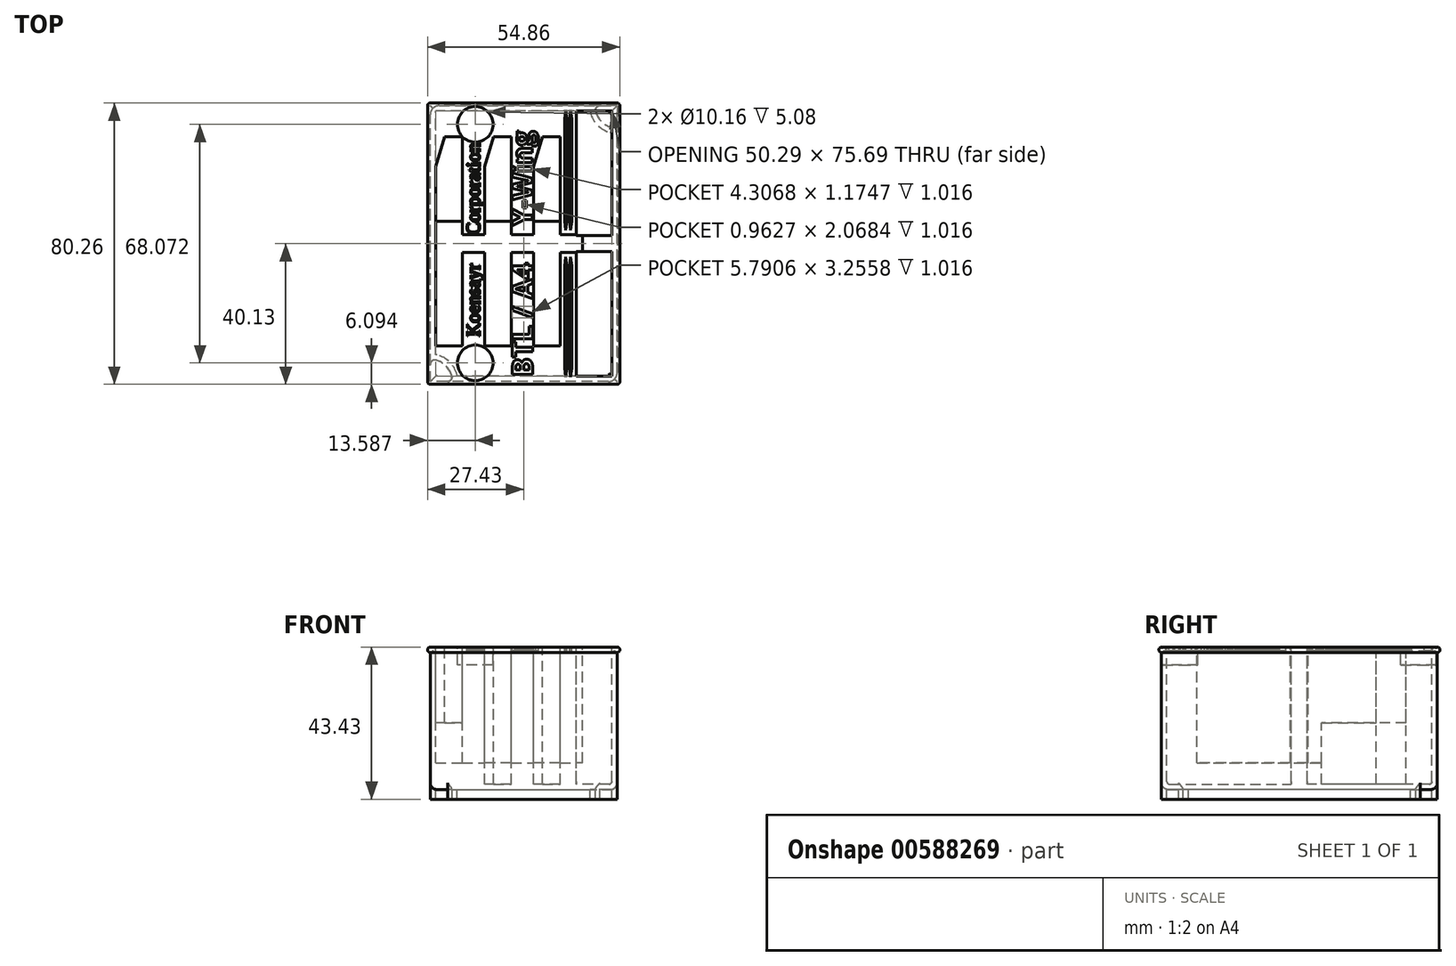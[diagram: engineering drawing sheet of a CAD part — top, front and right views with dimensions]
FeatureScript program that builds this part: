
annotation { "Feature Type Name" : "Feature", "Feature Type Description" : "" }
export const myFeature = defineFeature(function(context is Context, id is Id, definition is map)
    precondition{}
    {
        {
            var Q0;
            Q0=qCreatedBy(makeId("Front.planeOp"),FACE);
            var sketch = newSketch(context, id + "F0", { "sketchPlane" : qUnion([Q0])});
            skLineSegment(sketch, "E0.bottom", {"start": v(26.67, -20.32) * mm, "end": v(-26.67, -20.32) * mm});
            skLineSegment(sketch, "E0.top", {"start": v(26.67, 20.32) * mm, "end": v(-26.67, 20.32) * mm});
            skLineSegment(sketch, "E0.left", {"start": v(26.67, -20.32) * mm, "end": v(26.67, 20.32) * mm});
            skLineSegment(sketch, "E0.right", {"start": v(-26.67, -20.32) * mm, "end": v(-26.67, 20.32) * mm});
            skPoint(sketch, "E0.middle", {"position": v(0, 0) * mm});
            skSolve(sketch);
        }
        {
            var Q0;
            Q0=makeQuery(id+"F0.imprint","IMPRINT",FACE,{"disambiguationData":[TD([[makeQuery(id+"F0.imprint","IMPRINT",EDGE,{"derivedFrom":sQuery(id+"F0.wireOp",EDGE,"E0.bottom")}),-1.0]])]});
            extrude(context, id + "F1", {"entities" : qUnion([Q0]), "endBound" : BoundingType.SYMMETRIC, "depth" : 78.74 * mm});
        }
        {
            var Q0;
            Q0=makeQuery(id+"F1.opExtrude","SWEPT_FACE",FACE,{"disambiguationData":[OSD([sQuery(id+"F0.wireOp",EDGE,"E0.top")])]});
            shell(context, id + "F2", {"entities" : qUnion([Q0]), "thickness" : 1.52 * mm});
        }
        {
            var Q0;
            Q0=makeQuery(id+"F1.opExtrude","CAP_FACE",FACE,{"disambiguationData":[OSD([sQuery(id+"F0.wireOp",EDGE,"E0.bottom"),sQuery(id+"F0.wireOp",EDGE,"E0.top"),sQuery(id+"F0.wireOp",EDGE,"E0.left"),sQuery(id+"F0.wireOp",EDGE,"E0.right")])],"isStart":false});
            var sketch = newSketch(context, id + "F3", { "sketchPlane" : qUnion([Q0])});
            skArc(sketch, "E1", {"start": v(-26.67, 20.32) * mm, "mid": v(-27.43, 19.56) * mm, "end": v(-26.67, 18.8) * mm});
            skSolve(sketch);
        }
        {
            var Q0;
            {var subQ0=sQuery(id+"F3.wireOp",EDGE,"E1");Q0=makeQuery(id+"F3.imprint","IMPRINT",FACE,{"disambiguationData":[TD([[makeQuery(id+"F3.imprint","IMPRINT",EDGE,{"derivedFrom":subQ0}),1.0]])]});}
            var Q1;
            Q1=makeQuery(id+"F1.opExtrude","SWEPT_EDGE",EDGE,{"disambiguationData":[OSD([sQuery(id+"F0.wireOp",EDGE,"E0.top"),sQuery(id+"F0.wireOp",EDGE,"E0.right")])]});
            var Q2;
            Q2=makeQuery(id+"F1.opExtrude","CAP_EDGE",EDGE,{"disambiguationData":[OSD([sQuery(id+"F0.wireOp",EDGE,"E0.top")])],"isStart":true});
            var Q3;
            Q3=makeQuery(id+"F1.opExtrude","SWEPT_EDGE",EDGE,{"disambiguationData":[OSD([sQuery(id+"F0.wireOp",EDGE,"E0.top"),sQuery(id+"F0.wireOp",EDGE,"E0.left")])]});
            var Q4;
            Q4=makeQuery(id+"F1.opExtrude","CAP_EDGE",EDGE,{"disambiguationData":[OSD([sQuery(id+"F0.wireOp",EDGE,"E0.top")])],"isStart":false});
            sweep(context, id + "F4", {"operationType" : NewBodyOperationType.ADD, "profiles" : qUnion([Q0]), "path" : qUnion([Q1, Q2, Q3, Q4])});
        }
        {
            var Q0;
            Q0=makeQuery(id+"F1.opExtrude","SWEPT_FACE",FACE,{"disambiguationData":[OSD([sQuery(id+"F0.wireOp",EDGE,"E0.bottom")])]});
            var sketch = newSketch(context, id + "F5", { "sketchPlane" : qUnion([Q0])});
            skLineSegment(sketch, "E2.bottom", {"start": v(26.67, 39.37) * mm, "end": v(21.75, 39.37) * mm});
            skLineSegment(sketch, "E2.left", {"start": v(26.67, 39.37) * mm, "end": v(26.67, 34.45) * mm});
            skPoint(sketch, "E3.newPointA", {"position": v(20.32, 19.05) * mm});
            skArc(sketch, "E4", {"start": v(20.52, 37.78) * mm, "mid": v(22.18, 34.88) * mm, "end": v(25.08, 33.22) * mm});
            skPoint(sketch, "E5.visualSharp", {"position": v(20.32, 39.37) * mm});
            skArc(sketch, "E5.filletArc", {"start": v(21.75, 39.37) * mm, "mid": v(20.75, 38.88) * mm, "end": v(20.52, 37.78) * mm});
            skPoint(sketch, "E6.visualSharp", {"position": v(26.67, 33.02) * mm});
            skArc(sketch, "E6.filletArc", {"start": v(25.08, 33.22) * mm, "mid": v(26.18, 33.45) * mm, "end": v(26.67, 34.45) * mm});
            skArc(sketch, "E7.MirrorCS", {"start": v(-21.75, 39.37) * mm, "mid": v(-20.75, 38.88) * mm, "end": v(-20.52, 37.78) * mm});
            skArc(sketch, "E8.MirrorCS", {"start": v(-20.52, 37.78) * mm, "mid": v(-22.18, 34.88) * mm, "end": v(-25.08, 33.22) * mm});
            skArc(sketch, "E9.MirrorCS", {"start": v(-25.08, 33.22) * mm, "mid": v(-26.18, 33.45) * mm, "end": v(-26.67, 34.45) * mm});
            skLineSegment(sketch, "E10.MirrorCS", {"start": v(-26.67, 39.37) * mm, "end": v(-26.67, 34.45) * mm});
            skLineSegment(sketch, "E11.MirrorCS", {"start": v(-26.67, 39.37) * mm, "end": v(-21.75, 39.37) * mm});
            skArc(sketch, "E12.MirrorCS", {"start": v(-20.52, -37.78) * mm, "mid": v(-22.18, -34.88) * mm, "end": v(-25.08, -33.22) * mm});
            skArc(sketch, "E13.MirrorCS", {"start": v(-21.75, -39.37) * mm, "mid": v(-20.75, -38.88) * mm, "end": v(-20.52, -37.78) * mm});
            skLineSegment(sketch, "E14.MirrorCS", {"start": v(-26.67, -39.37) * mm, "end": v(-21.75, -39.37) * mm});
            skLineSegment(sketch, "E15.MirrorCS", {"start": v(-26.67, -39.37) * mm, "end": v(-26.67, -34.45) * mm});
            skArc(sketch, "E16.MirrorCS", {"start": v(-25.08, -33.22) * mm, "mid": v(-26.18, -33.45) * mm, "end": v(-26.67, -34.45) * mm});
            skArc(sketch, "E17.MirrorCS", {"start": v(21.75, -39.37) * mm, "mid": v(20.75, -38.88) * mm, "end": v(20.52, -37.78) * mm});
            skArc(sketch, "E18.MirrorCS", {"start": v(20.52, -37.78) * mm, "mid": v(22.18, -34.88) * mm, "end": v(25.08, -33.22) * mm});
            skArc(sketch, "E19.MirrorCS", {"start": v(25.08, -33.22) * mm, "mid": v(26.18, -33.45) * mm, "end": v(26.67, -34.45) * mm});
            skLineSegment(sketch, "E20.MirrorCS", {"start": v(26.67, -39.37) * mm, "end": v(26.67, -34.45) * mm});
            skLineSegment(sketch, "E21.MirrorCS", {"start": v(26.67, -39.37) * mm, "end": v(21.75, -39.37) * mm});
            skSolve(sketch);
        }
        {
            var Q0;
            Q0=makeQuery(id+"F5.imprint","IMPRINT",FACE,{"disambiguationData":[TD([[makeQuery(id+"F5.imprint","IMPRINT",EDGE,{"derivedFrom":sQuery(id+"F5.wireOp",EDGE,"E2.bottom")}),1.0]])]});
            var Q1;
            Q1=makeQuery(id+"F5.imprint","IMPRINT",FACE,{"disambiguationData":[TD([[makeQuery(id+"F5.imprint","IMPRINT",EDGE,{"derivedFrom":sQuery(id+"F5.wireOp",EDGE,"E8.MirrorCS")}),-1.0]])]});
            var Q2;
            Q2=makeQuery(id+"F5.imprint","IMPRINT",FACE,{"disambiguationData":[TD([[makeQuery(id+"F5.imprint","IMPRINT",EDGE,{"derivedFrom":sQuery(id+"F5.wireOp",EDGE,"E12.MirrorCS")}),1.0]])]});
            var Q3;
            Q3=makeQuery(id+"F5.imprint","IMPRINT",FACE,{"disambiguationData":[TD([[makeQuery(id+"F5.imprint","IMPRINT",EDGE,{"derivedFrom":sQuery(id+"F5.wireOp",EDGE,"E17.MirrorCS")}),-1.0]])]});
            extrude(context, id + "F6", {"entities" : qUnion([Q0, Q1, Q2, Q3]), "operationType" : NewBodyOperationType.ADD, "depth" : 2.8 * mm});
        }
        {
            var Q0;
            Q0=makeQuery(id+"F6.opExtrude","CAP_FACE",FACE,{"disambiguationData":[OSD([sQuery(id+"F5.wireOp",EDGE,"E2.bottom"),sQuery(id+"F5.wireOp",EDGE,"E2.left"),sQuery(id+"F5.wireOp",EDGE,"E4"),sQuery(id+"F5.wireOp",EDGE,"E5.filletArc"),sQuery(id+"F5.wireOp",EDGE,"E6.filletArc")])],"isStart":false});
            var Q1;
            Q1=makeQuery(id+"F6.opExtrude","CAP_FACE",FACE,{"disambiguationData":[OSD([sQuery(id+"F5.wireOp",EDGE,"E8.MirrorCS"),sQuery(id+"F5.wireOp",EDGE,"E9.MirrorCS"),sQuery(id+"F5.wireOp",EDGE,"E10.MirrorCS"),sQuery(id+"F5.wireOp",EDGE,"E7.MirrorCS"),sQuery(id+"F5.wireOp",EDGE,"E11.MirrorCS")])],"isStart":false});
            var Q2;
            Q2=makeQuery(id+"F6.opExtrude","CAP_FACE",FACE,{"disambiguationData":[OSD([sQuery(id+"F5.wireOp",EDGE,"E12.MirrorCS"),sQuery(id+"F5.wireOp",EDGE,"E13.MirrorCS"),sQuery(id+"F5.wireOp",EDGE,"E14.MirrorCS"),sQuery(id+"F5.wireOp",EDGE,"E15.MirrorCS"),sQuery(id+"F5.wireOp",EDGE,"E16.MirrorCS")])],"isStart":false});
            var Q3;
            Q3=makeQuery(id+"F6.opExtrude","CAP_FACE",FACE,{"disambiguationData":[OSD([sQuery(id+"F5.wireOp",EDGE,"E17.MirrorCS"),sQuery(id+"F5.wireOp",EDGE,"E18.MirrorCS"),sQuery(id+"F5.wireOp",EDGE,"E19.MirrorCS"),sQuery(id+"F5.wireOp",EDGE,"E20.MirrorCS"),sQuery(id+"F5.wireOp",EDGE,"E21.MirrorCS")])],"isStart":false});
            shell(context, id + "F7", {"entities" : qUnion([Q0, Q1, Q2, Q3]), "thickness" : 1.52 * mm});
        }
        {
            var Q0;
            Q0=makeQuery(id+"F2.opShell","OFFSET_FACE",FACE,{"disambiguationData":[OSD([sQuery(id+"F0.wireOp",EDGE,"E0.bottom")])]});
            fillet(context, id + "F8", {"entities" : qUnion([Q0]), "radius" : 0.76 * mm, "tangentPropagation" : true, "allowEdgeOverflow" : false});
        }
        {
            var Q0;
            Q0=makeQuery(id+"F1.opExtrude","SWEPT_EDGE",EDGE,{"disambiguationData":[OSD([sQuery(id+"F0.wireOp",EDGE,"E0.bottom"),sQuery(id+"F0.wireOp",EDGE,"E0.right")])]});
            var Q1;
            Q1=makeQuery(id+"F1.opExtrude","CAP_EDGE",EDGE,{"disambiguationData":[OSD([sQuery(id+"F0.wireOp",EDGE,"E0.bottom")])],"isStart":false});
            var Q2;
            Q2=makeQuery(id+"F1.opExtrude","SWEPT_EDGE",EDGE,{"disambiguationData":[OSD([sQuery(id+"F0.wireOp",EDGE,"E0.bottom"),sQuery(id+"F0.wireOp",EDGE,"E0.left")])]});
            var Q3;
            Q3=makeQuery(id+"F1.opExtrude","CAP_EDGE",EDGE,{"disambiguationData":[OSD([sQuery(id+"F0.wireOp",EDGE,"E0.bottom")])],"isStart":true});
            fillet(context, id + "F9", {"entities" : qUnion([Q0, Q1, Q2, Q3]), "radius" : 1.9 * mm, "tangentPropagation" : true, "allowEdgeOverflow" : false});
        }
        {
            var Q0;
            Q0=makeQuery(id+"F4.opSweep","MID_CAP_EDGE",EDGE,{"disambiguationData":[OSD([sQuery(id+"F0.wireOp",EDGE,"E0.top"),sQuery(id+"F0.wireOp",EDGE,"E0.left"),sQuery(id+"F3.wireOp",EDGE,"E1")])],"capPos":3.0});
            var Q1;
            Q1=makeQuery(id+"F4.opSweep","MID_CAP_EDGE",EDGE,{"disambiguationData":[OSD([sQuery(id+"F0.wireOp",EDGE,"E0.top"),sQuery(id+"F0.wireOp",EDGE,"E0.left"),sQuery(id+"F3.wireOp",EDGE,"E1")])],"capPos":2.0});
            var Q2;
            Q2=makeQuery(id+"F4.opSweep","MID_CAP_EDGE",EDGE,{"disambiguationData":[OSD([sQuery(id+"F0.wireOp",EDGE,"E0.top"),sQuery(id+"F0.wireOp",EDGE,"E0.right"),sQuery(id+"F3.wireOp",EDGE,"E1")])],"capPos":1.0});
            var Q3;
            Q3=makeQuery(id+"F4.opSweep","CAP_EDGE",EDGE,{"disambiguationData":[OSD([sQuery(id+"F0.wireOp",EDGE,"E0.top"),sQuery(id+"F0.wireOp",EDGE,"E0.right"),sQuery(id+"F3.wireOp",EDGE,"E1")])],"isStart":true});
            fillet(context, id + "F10", {"entities" : qUnion([Q0, Q1, Q2, Q3]), "radius" : 0.76 * mm, "tangentPropagation" : true, "allowEdgeOverflow" : false});
        }
        {
            var Q0;
            Q0=makeQuery(id+"F6.boolean.opBoolean","MERGE",EDGE,{"derivedFrom":[makeQuery(id+"F1.opExtrude","CAP_EDGE",EDGE,{"disambiguationData":[OSD([sQuery(id+"F0.wireOp",EDGE,"E0.left")])],"isStart":false}),makeQuery(id+"F6.opExtrude","SWEPT_EDGE",EDGE,{"disambiguationData":[OSD([sQuery(id+"F5.wireOp",EDGE,"E2.bottom"),sQuery(id+"F5.wireOp",EDGE,"E2.left")])]})]});
            var Q1;
            Q1=makeQuery(id+"F6.boolean.opBoolean","MERGE",EDGE,{"derivedFrom":[makeQuery(id+"F1.opExtrude","CAP_EDGE",EDGE,{"disambiguationData":[OSD([sQuery(id+"F0.wireOp",EDGE,"E0.left")])],"isStart":true}),makeQuery(id+"F6.opExtrude","SWEPT_EDGE",EDGE,{"disambiguationData":[OSD([sQuery(id+"F5.wireOp",EDGE,"E20.MirrorCS"),sQuery(id+"F5.wireOp",EDGE,"E21.MirrorCS")])]})]});
            var Q2;
            Q2=makeQuery(id+"F6.boolean.opBoolean","MERGE",EDGE,{"derivedFrom":[makeQuery(id+"F1.opExtrude","CAP_EDGE",EDGE,{"disambiguationData":[OSD([sQuery(id+"F0.wireOp",EDGE,"E0.right")])],"isStart":false}),makeQuery(id+"F6.opExtrude","SWEPT_EDGE",EDGE,{"disambiguationData":[OSD([sQuery(id+"F5.wireOp",EDGE,"E10.MirrorCS"),sQuery(id+"F5.wireOp",EDGE,"E11.MirrorCS")])]})]});
            var Q3;
            Q3=makeQuery(id+"F6.boolean.opBoolean","MERGE",EDGE,{"derivedFrom":[makeQuery(id+"F1.opExtrude","CAP_EDGE",EDGE,{"disambiguationData":[OSD([sQuery(id+"F0.wireOp",EDGE,"E0.right")])],"isStart":true}),makeQuery(id+"F6.opExtrude","SWEPT_EDGE",EDGE,{"disambiguationData":[OSD([sQuery(id+"F5.wireOp",EDGE,"E14.MirrorCS"),sQuery(id+"F5.wireOp",EDGE,"E15.MirrorCS")])]})]});
            fillet(context, id + "F11", {"entities" : qUnion([Q0, Q1, Q2, Q3]), "radius" : 2.54 * mm, "tangentPropagation" : true, "allowEdgeOverflow" : false});
        }
        {
            var Q0;
            Q0=makeQuery(id+"F1.opExtrude","SWEPT_BODY",BODY,{"disambiguationData":[OSD([sQuery(id+"F0.wireOp",EDGE,"E0.bottom"),sQuery(id+"F0.wireOp",EDGE,"E0.top"),sQuery(id+"F0.wireOp",EDGE,"E0.left"),sQuery(id+"F0.wireOp",EDGE,"E0.right")])]});
            transform(context, id + "F12", {"entities" : qUnion([Q0]), "transformType" : TransformType.COPY});
        }
        {
            var Q0;
            Q0=makeQuery(id+"F12.opPattern","COPY",BODY,{"derivedFrom":makeQuery(id+"F1.opExtrude","SWEPT_BODY",BODY,{"disambiguationData":[OSD([sQuery(id+"F0.wireOp",EDGE,"E0.bottom"),sQuery(id+"F0.wireOp",EDGE,"E0.top"),sQuery(id+"F0.wireOp",EDGE,"E0.left"),sQuery(id+"F0.wireOp",EDGE,"E0.right")])]}),"instanceName":"1"});
            deleteBodies(context, id + "F13", {"entities" : qUnion([Q0])});
        }
        {
            var Q0;
            Q0=makeQuery(id+"F1.opExtrude","SWEPT_FACE",FACE,{"disambiguationData":[OSD([sQuery(id+"F0.wireOp",EDGE,"E0.top")])]});
            var sketch = newSketch(context, id + "F14", { "sketchPlane" : qUnion([Q0])});
            skPoint(sketch, "E22", {"position": v(-25.15, 30.48) * mm});
            skLineSegment(sketch, "E23.bottom", {"start": v(-22.6, 30.48) * mm, "end": v(-17.53, 30.48) * mm});
            skLineSegment(sketch, "E23.top", {"start": v(-25.15, -29.21) * mm, "end": v(-17.53, -29.21) * mm});
            skLineSegment(sketch, "E23.left", {"start": v(-25.15, 21.96) * mm, "end": v(-25.15, -29.21) * mm});
            skLineSegment(sketch, "E23.right", {"start": v(-17.53, 30.48) * mm, "end": v(-17.53, 2.54) * mm});
            skLineSegment(sketch, "E24.bottom", {"start": v(-17.53, 2.54) * mm, "end": v(-11.18, 2.54) * mm});
            skLineSegment(sketch, "E24.top", {"start": v(-17.53, -2.54) * mm, "end": v(-11.18, -2.54) * mm});
            skLineSegment(sketch, "E24.right", {"start": v(-11.18, 2.54) * mm, "end": v(-11.18, -2.54) * mm});
            skLineSegment(sketch, "E25.trimOffspring", {"start": v(-17.53, -2.54) * mm, "end": v(-17.53, -29.21) * mm});
            skLineSegment(sketch, "E26", {"start": v(-17.53, 2.54) * mm, "end": v(-17.53, 6.35) * mm});
            skLineSegment(sketch, "E27", {"start": v(-17.53, 6.35) * mm, "end": v(-25.15, 6.35) * mm});
            skPoint(sketch, "E28", {"position": v(-11.18, 30.48) * mm});
            skLineSegment(sketch, "E29.bottom", {"start": v(-8.64, 30.48) * mm, "end": v(-3.56, 30.48) * mm});
            skLineSegment(sketch, "E29.top", {"start": v(-11.18, -29.2) * mm, "end": v(-3.56, -29.2) * mm});
            skLineSegment(sketch, "E29.left", {"start": v(-11.18, 21.96) * mm, "end": v(-11.18, -29.2) * mm});
            skLineSegment(sketch, "E29.right", {"start": v(-3.56, 30.48) * mm, "end": v(-3.56, 2.54) * mm});
            skLineSegment(sketch, "E30.bottom", {"start": v(-3.56, 2.54) * mm, "end": v(2.8, 2.54) * mm});
            skLineSegment(sketch, "E30.top", {"start": v(-3.56, -2.54) * mm, "end": v(2.8, -2.54) * mm});
            skLineSegment(sketch, "E30.right", {"start": v(2.8, 2.54) * mm, "end": v(2.8, -2.54) * mm});
            skLineSegment(sketch, "E31.trimOffspring", {"start": v(-3.56, -2.54) * mm, "end": v(-3.56, -29.2) * mm});
            skLineSegment(sketch, "E32", {"start": v(-3.56, 2.54) * mm, "end": v(-3.56, 6.35) * mm});
            skLineSegment(sketch, "E33", {"start": v(-3.56, 6.35) * mm, "end": v(-11.18, 6.35) * mm});
            skPoint(sketch, "E34", {"position": v(2.8, 30.48) * mm});
            skLineSegment(sketch, "E35.bottom", {"start": v(5.33, 30.48) * mm, "end": v(10.41, 30.48) * mm});
            skLineSegment(sketch, "E35.top", {"start": v(2.8, -29.2) * mm, "end": v(10.41, -29.2) * mm});
            skLineSegment(sketch, "E35.left", {"start": v(2.8, 21.96) * mm, "end": v(2.8, -29.2) * mm});
            skLineSegment(sketch, "E35.right", {"start": v(10.41, 30.48) * mm, "end": v(10.41, 2.54) * mm});
            skLineSegment(sketch, "E36.bottom", {"start": v(10.41, 2.54) * mm, "end": v(16.76, 2.54) * mm});
            skLineSegment(sketch, "E36.top", {"start": v(10.41, -2.54) * mm, "end": v(16.76, -2.54) * mm});
            skLineSegment(sketch, "E37.trimOffspring", {"start": v(10.41, -2.54) * mm, "end": v(10.41, -29.2) * mm});
            skLineSegment(sketch, "E38", {"start": v(10.41, 2.54) * mm, "end": v(10.41, 6.35) * mm});
            skLineSegment(sketch, "E39", {"start": v(10.41, 6.35) * mm, "end": v(2.8, 6.35) * mm});
            skLineSegment(sketch, "E40", {"start": v(16.76, 2.54) * mm, "end": v(16.76, -2.54) * mm});
            skPoint(sketch, "E41.0", {"position": v(25.15, 37.85) * mm});
            skPoint(sketch, "E41.1", {"position": v(25.15, -37.85) * mm});
            skLineSegment(sketch, "E42.bottom", {"start": v(25.15, 37.85) * mm, "end": v(14.99, 37.85) * mm});
            skLineSegment(sketch, "E42.top", {"start": v(25.15, 2.29) * mm, "end": v(14.99, 2.29) * mm});
            skLineSegment(sketch, "E42.left", {"start": v(25.15, 37.85) * mm, "end": v(25.15, 2.29) * mm});
            skLineSegment(sketch, "E42.right", {"start": v(14.99, 37.85) * mm, "end": v(14.99, 2.29) * mm});
            skLineSegment(sketch, "E43.bottom", {"start": v(25.15, -37.85) * mm, "end": v(14.99, -37.85) * mm});
            skLineSegment(sketch, "E43.top", {"start": v(25.15, -2.29) * mm, "end": v(14.99, -2.29) * mm});
            skLineSegment(sketch, "E43.left", {"start": v(25.15, -37.85) * mm, "end": v(25.15, -2.29) * mm});
            skLineSegment(sketch, "E43.right", {"start": v(14.99, -37.85) * mm, "end": v(14.99, -2.29) * mm});
            skPoint(sketch, "E44.middle", {"position": v(0, 0.64) * mm});
            skLineSegment(sketch, "E45.0", {"start": v(25.15, -37.85) * mm, "end": v(-25.15, -37.85) * mm});
            skLineSegment(sketch, "E46", {"start": v(-17.53, 30.48) * mm, "end": v(-22.6, 30.48) * mm});
            skLineSegment(sketch, "E47", {"start": v(-22.6, 30.48) * mm, "end": v(-25.15, 21.96) * mm});
            skLineSegment(sketch, "E48", {"start": v(-3.56, 30.48) * mm, "end": v(-7.37, 30.48) * mm});
            skLineSegment(sketch, "E49", {"start": v(-3.56, 30.48) * mm, "end": v(-8.64, 30.48) * mm});
            skLineSegment(sketch, "E50", {"start": v(-8.64, 30.48) * mm, "end": v(-11.18, 21.96) * mm});
            skLineSegment(sketch, "E51", {"start": v(10.41, 30.48) * mm, "end": v(5.33, 30.48) * mm});
            skLineSegment(sketch, "E52", {"start": v(5.33, 30.48) * mm, "end": v(2.8, 21.96) * mm});
            skLineSegment(sketch, "E53.bottom", {"start": v(-25.15, -37.85) * mm, "end": v(25.15, -37.85) * mm});
            skLineSegment(sketch, "E53.top", {"start": v(-25.15, 37.85) * mm, "end": v(25.15, 37.85) * mm});
            skLineSegment(sketch, "E53.left", {"start": v(-25.15, -37.85) * mm, "end": v(-25.15, 37.85) * mm});
            skLineSegment(sketch, "E53.right", {"start": v(25.15, -37.85) * mm, "end": v(25.15, 37.85) * mm});
            skSolve(sketch);
        }
        {
            var Q0;
            Q0=makeQuery(id+"F14.imprint","IMPRINT",FACE,{"disambiguationData":[TD([[makeQuery(id+"F14.imprint","IMPRINT",EDGE,{"derivedFrom":sQuery(id+"F14.wireOp",EDGE,"E23.right")}),1.0]])]});
            var Q1;
            {var subQ6=sQuery(id+"F14.wireOp",EDGE,"E23.top");Q1=makeQuery(id+"F14.imprint","IMPRINT",FACE,{"disambiguationData":[TD([[makeQuery(id+"F14.imprint","IMPRINT",EDGE,{"derivedFrom":subQ6}),-1.0]])]});}
            var Q2;
            Q2=makeQuery(id+"F14.imprint","IMPRINT",FACE,{"disambiguationData":[TD([[makeQuery(id+"F14.imprint","IMPRINT",EDGE,{"derivedFrom":sQuery(id+"F14.wireOp",EDGE,"E23.right")}),-1.0]])]});
            var Q3;
            {var subQ1=sQuery(id+"F14.wireOp",EDGE,"E29.right");Q3=makeQuery(id+"F14.imprint","IMPRINT",FACE,{"disambiguationData":[TD([[makeQuery(id+"F14.imprint","IMPRINT",EDGE,{"derivedFrom":subQ1}),-1.0]])]});}
            var Q4;
            Q4=makeQuery(id+"F14.imprint","IMPRINT",FACE,{"disambiguationData":[TD([[makeQuery(id+"F14.imprint","IMPRINT",EDGE,{"derivedFrom":sQuery(id+"F14.wireOp",EDGE,"E35.right")}),-1.0]])]});
            var Q5;
            {var subQ4=sQuery(id+"F14.wireOp",EDGE,"E35.top");Q5=makeQuery(id+"F14.imprint","IMPRINT",FACE,{"disambiguationData":[TD([[makeQuery(id+"F14.imprint","IMPRINT",EDGE,{"derivedFrom":subQ4}),1.0]])]});}
            var Q6;
            {var subQ1=sQuery(id+"F14.wireOp",EDGE,"E23.top");Q6=makeQuery(id+"F14.imprint","IMPRINT",FACE,{"disambiguationData":[TD([[makeQuery(id+"F14.imprint","IMPRINT",EDGE,{"derivedFrom":subQ1}),1.0]])]});}
            var Q7;
            {var subQ0=sQuery(id+"F14.wireOp",EDGE,"E40");Q7=makeQuery(id+"F14.imprint","IMPRINT",FACE,{"disambiguationData":[TD([[makeQuery(id+"F14.imprint","IMPRINT",EDGE,{"derivedFrom":subQ0}),1.0]])]});}
            var Q8;
            {var subQ2=sQuery(id+"F14.wireOp",EDGE,"E29.top");Q8=makeQuery(id+"F14.imprint","IMPRINT",FACE,{"disambiguationData":[TD([[makeQuery(id+"F14.imprint","IMPRINT",EDGE,{"derivedFrom":subQ2}),1.0]])]});}
            extrude(context, id + "F15", {"entities" : qUnion([Q0, Q1, Q2, Q3, Q4, Q5, Q6, Q7, Q8]), "operationType" : NewBodyOperationType.ADD, "endBound" : BoundingType.UP_TO_NEXT, "oppositeDirection" : true, "depth" : 25.4 * mm, "offsetDistance" : 25.4 * mm});
        }
        {
            var Q0;
            {var subQ1=sQuery(id+"F14.wireOp",EDGE,"E23.top");Q0=makeQuery(id+"F14.imprint","IMPRINT",FACE,{"disambiguationData":[TD([[makeQuery(id+"F14.imprint","IMPRINT",EDGE,{"derivedFrom":subQ1}),1.0]])]});}
            var Q1;
            {var subQ2=sQuery(id+"F14.wireOp",EDGE,"E29.top");Q1=makeQuery(id+"F14.imprint","IMPRINT",FACE,{"disambiguationData":[TD([[makeQuery(id+"F14.imprint","IMPRINT",EDGE,{"derivedFrom":subQ2}),1.0]])]});}
            var Q2;
            {var subQ4=sQuery(id+"F14.wireOp",EDGE,"E35.top");Q2=makeQuery(id+"F14.imprint","IMPRINT",FACE,{"disambiguationData":[TD([[makeQuery(id+"F14.imprint","IMPRINT",EDGE,{"derivedFrom":subQ4}),1.0]])]});}
            extrude(context, id + "F16", {"entities" : qUnion([Q0, Q1, Q2]), "operationType" : NewBodyOperationType.REMOVE, "oppositeDirection" : true, "depth" : 33.02 * mm, "offsetDistance" : 25.4 * mm});
        }
        {
            var Q0;
            Q0=makeQuery(id+"F14.imprint","IMPRINT",FACE,{"disambiguationData":[TD([[makeQuery(id+"F14.imprint","IMPRINT",EDGE,{"derivedFrom":sQuery(id+"F14.wireOp",EDGE,"E23.right")}),-1.0]])]});
            var Q1;
            {var subQ1=sQuery(id+"F14.wireOp",EDGE,"E29.right");Q1=makeQuery(id+"F14.imprint","IMPRINT",FACE,{"disambiguationData":[TD([[makeQuery(id+"F14.imprint","IMPRINT",EDGE,{"derivedFrom":subQ1}),-1.0]])]});}
            var Q2;
            Q2=makeQuery(id+"F14.imprint","IMPRINT",FACE,{"disambiguationData":[TD([[makeQuery(id+"F14.imprint","IMPRINT",EDGE,{"derivedFrom":sQuery(id+"F14.wireOp",EDGE,"E35.right")}),-1.0]])]});
            extrude(context, id + "F17", {"entities" : qUnion([Q0, Q1, Q2]), "operationType" : NewBodyOperationType.REMOVE, "oppositeDirection" : true, "depth" : 21.59 * mm, "offsetDistance" : 25.4 * mm});
        }
        {
            var Q0;
            Q0=makeQuery(id+"F15.boolean.opBoolean","MERGE",FACE,{"derivedFrom":[makeQuery(id+"F1.opExtrude","SWEPT_FACE",FACE,{"disambiguationData":[OSD([sQuery(id+"F0.wireOp",EDGE,"E0.top")])]}),makeQuery(id+"F15.opExtrude","CAP_FACE",FACE,{"disambiguationData":[OSD([sQuery(id+"F14.wireOp",EDGE,"E42.top"),sQuery(id+"F14.wireOp",EDGE,"E42.right"),sQuery(id+"F14.wireOp",EDGE,"E43.top"),sQuery(id+"F14.wireOp",EDGE,"E43.right"),sQuery(id+"F14.wireOp",EDGE,"E53.bottom"),sQuery(id+"F14.wireOp",EDGE,"E53.top"),sQuery(id+"F14.wireOp",EDGE,"E53.left"),sQuery(id+"F14.wireOp",EDGE,"E53.right")])],"isStart":true})]});
            var sketch = newSketch(context, id + "F18", { "sketchPlane" : qUnion([Q0])});
            skLineSegment(sketch, "E54.0", {"start": v(26.92, -39.37) * mm, "end": v(-26.42, -39.37) * mm});
            skLineSegment(sketch, "E55.2", {"start": v(26.67, 39.37) * mm, "end": v(-26.67, 39.37) * mm});
            skCircle(sketch, "E56", {"center": v(-13.84, -34.04) * mm, "radius": 5.08 * mm});
            skCircle(sketch, "E57", {"center": v(-13.84, 34.04) * mm, "radius": 5.08 * mm});
            skSolve(sketch);
        }
        {
            var Q0;
            Q0 = qSketchRegion(id + "F18", true);
            extrude(context, id + "F19", {"entities" : qUnion([Q0]), "operationType" : NewBodyOperationType.REMOVE, "oppositeDirection" : true, "depth" : 5.08 * mm, "offsetDistance" : 25.4 * mm});
        }
        {
            var Q0;
            Q0=makeQuery(id+"F15.boolean.opBoolean","MERGE",FACE,{"derivedFrom":[makeQuery(id+"F1.opExtrude","SWEPT_FACE",FACE,{"disambiguationData":[OSD([sQuery(id+"F0.wireOp",EDGE,"E0.top")])]}),makeQuery(id+"F15.opExtrude","CAP_FACE",FACE,{"disambiguationData":[OSD([sQuery(id+"F14.wireOp",EDGE,"E42.top"),sQuery(id+"F14.wireOp",EDGE,"E42.right"),sQuery(id+"F14.wireOp",EDGE,"E43.top"),sQuery(id+"F14.wireOp",EDGE,"E43.right"),sQuery(id+"F14.wireOp",EDGE,"E53.bottom"),sQuery(id+"F14.wireOp",EDGE,"E53.top"),sQuery(id+"F14.wireOp",EDGE,"E53.left"),sQuery(id+"F14.wireOp",EDGE,"E53.right")])],"isStart":true})]});
            var sketch = newSketch(context, id + "F20", { "sketchPlane" : qUnion([Q0])});
            skText(sketch, "E58", { "text": "Y-Wing", "fontName": "OpenSans-Bold.ttf"});
            skText(sketch, "E59", { "text": "BTL / A4", "fontName": "OpenSans-Bold.ttf"});
            skText(sketch, "E60", { "text": "Y-Wing", "fontName": "OpenSans-Bold.ttf"});
            skText(sketch, "E61", { "text": "Koensayr", "fontName": "Tinos-Regular.ttf"});
            skText(sketch, "E62", { "text": "Corporation", "fontName": "Tinos-Regular.ttf"});
            skPoint(sketch, "E63.endSnap0", {"position": v(-14.55, -23.65) * mm});
            const initialGuessF20  = {"E58": [0.0026, 0.06217, 0, 1, 0.00574], "E59": [0.00254, -0.03801, 0, 1, 0.00584], "E60": [0.00238, 0.00508, 0, 1, 0.00568], "E61": [-0.0126, -0.02651, 0, 1, 0.00391], "E62": [-0.0126, 0.00254, 0, 1, 0.00391]};
            skSetInitialGuess(sketch, initialGuessF20);
            skSolve(sketch);
        }
        {
            var Q0;
            Q0 = qSketchRegion(id + "F20", true);
            extrude(context, id + "F21", {"entities" : qUnion([Q0]), "operationType" : NewBodyOperationType.REMOVE, "oppositeDirection" : true, "depth" : 1.02 * mm, "offsetDistance" : 25.4 * mm});
        }
        {
            var Q0;
            {var subQ0=sQuery(id+"F14.wireOp",EDGE,"E43.right");var subQ1=sQuery(id+"F14.wireOp",EDGE,"E43.top");var subQ2=sQuery(id+"F14.wireOp",EDGE,"E42.right");var subQ3=sQuery(id+"F14.wireOp",EDGE,"E42.top");var subQ6=sQuery(id+"F0.wireOp",EDGE,"E0.top");var subQ8=sQuery(id+"F0.wireOp",EDGE,"E0.left");var subQ17=sQuery(id+"F14.wireOp",EDGE,"E53.left");Q0=makeQuery(id+"F21.boolean.opBoolean","SPLIT",FACE,{"disambiguationData":[TD([makeQuery(id+"F2.opShell","OFFSET_FACE",FACE,{"disambiguationData":[OSD([subQ8])]})])],"derivedFrom":makeQuery(id+"F15.boolean.opBoolean","MERGE",FACE,{"derivedFrom":[makeQuery(id+"F1.opExtrude","SWEPT_FACE",FACE,{"disambiguationData":[OSD([subQ6])]}),makeQuery(id+"F15.opExtrude","CAP_FACE",FACE,{"disambiguationData":[OSD([subQ3,subQ2,subQ1,subQ0,sQuery(id+"F14.wireOp",EDGE,"E53.bottom"),sQuery(id+"F14.wireOp",EDGE,"E53.top"),subQ17,sQuery(id+"F14.wireOp",EDGE,"E53.right")])],"isStart":true})]})});}
            var sketch = newSketch(context, id + "F22", { "sketchPlane" : qUnion([Q0])});
            skLineSegment(sketch, "E64.left", {"start": v(11.68, -6.33) * mm, "end": v(11.68, -35.58) * mm});
            skLineSegment(sketch, "E64.right", {"start": v(12.32, -6.33) * mm, "end": v(12.32, -35.58) * mm});
            skLineSegment(sketch, "E65.left", {"start": v(13.72, -6.33) * mm, "end": v(13.72, -35.58) * mm});
            skLineSegment(sketch, "E65.right", {"start": v(13.08, -6.33) * mm, "end": v(13.08, -35.58) * mm});
            skLineSegment(sketch, "E66", {"start": v(12, -38.1) * mm, "end": v(11.68, -35.58) * mm});
            skLineSegment(sketch, "E67", {"start": v(12, -38.1) * mm, "end": v(12.32, -35.58) * mm});
            skLineSegment(sketch, "E68", {"start": v(13.4, -38.1) * mm, "end": v(13.08, -35.58) * mm});
            skLineSegment(sketch, "E69", {"start": v(13.4, -38.1) * mm, "end": v(13.72, -35.58) * mm});
            skPoint(sketch, "E70.orphan", {"position": v(11.68, -38.1) * mm});
            skPoint(sketch, "E71.orphan", {"position": v(12.32, -38.1) * mm});
            skPoint(sketch, "E72.orphan", {"position": v(13.72, -38.1) * mm});
            skPoint(sketch, "E65.top.end.orphan", {"position": v(13.08, -38.1) * mm});
            skLineSegment(sketch, "E73", {"start": v(12, -3.8) * mm, "end": v(11.68, -6.33) * mm});
            skLineSegment(sketch, "E74", {"start": v(12, -3.8) * mm, "end": v(12.32, -6.33) * mm});
            skLineSegment(sketch, "E75", {"start": v(13.4, -3.8) * mm, "end": v(13.08, -6.33) * mm});
            skLineSegment(sketch, "E76", {"start": v(13.4, -3.8) * mm, "end": v(13.72, -6.33) * mm});
            skPoint(sketch, "E77.orphan", {"position": v(11.68, -3.8) * mm});
            skPoint(sketch, "E78.orphan", {"position": v(12.32, -3.8) * mm});
            skPoint(sketch, "E79.orphan", {"position": v(13.08, -3.8) * mm});
            skPoint(sketch, "E80.orphan", {"position": v(13.72, -3.8) * mm});
            skLineSegment(sketch, "E81.MirrorCS", {"start": v(12, 38.1) * mm, "end": v(11.68, 35.58) * mm});
            skLineSegment(sketch, "E82.MirrorCS", {"start": v(12, 38.1) * mm, "end": v(12.32, 35.58) * mm});
            skLineSegment(sketch, "E83.MirrorCS", {"start": v(13.4, 38.1) * mm, "end": v(13.08, 35.58) * mm});
            skLineSegment(sketch, "E84.MirrorCS", {"start": v(13.4, 38.1) * mm, "end": v(13.72, 35.58) * mm});
            skLineSegment(sketch, "E85.MirrorCS", {"start": v(12, 3.8) * mm, "end": v(11.68, 6.33) * mm});
            skLineSegment(sketch, "E86.MirrorCS", {"start": v(12, 3.8) * mm, "end": v(12.32, 6.33) * mm});
            skLineSegment(sketch, "E87.MirrorCS", {"start": v(13.4, 3.8) * mm, "end": v(13.08, 6.33) * mm});
            skLineSegment(sketch, "E88.MirrorCS", {"start": v(13.4, 3.8) * mm, "end": v(13.72, 6.33) * mm});
            skPoint(sketch, "E89.MirrorP", {"position": v(13.08, 3.8) * mm});
            skPoint(sketch, "E90.MirrorP", {"position": v(11.68, 3.8) * mm});
            skPoint(sketch, "E91.MirrorP", {"position": v(12.32, 3.8) * mm});
            skLineSegment(sketch, "E92.MirrorCS", {"start": v(11.68, 6.33) * mm, "end": v(11.68, 35.58) * mm});
            skLineSegment(sketch, "E93.MirrorCS", {"start": v(12.32, 6.33) * mm, "end": v(12.32, 35.58) * mm});
            skLineSegment(sketch, "E94.MirrorCS", {"start": v(13.08, 6.33) * mm, "end": v(13.08, 35.58) * mm});
            skLineSegment(sketch, "E95.MirrorCS", {"start": v(13.72, 6.33) * mm, "end": v(13.72, 35.58) * mm});
            skPoint(sketch, "E96.MirrorP", {"position": v(13.08, 38.1) * mm});
            skPoint(sketch, "E97.MirrorP", {"position": v(11.68, 38.1) * mm});
            skPoint(sketch, "E98.MirrorP", {"position": v(13.72, 3.8) * mm});
            skPoint(sketch, "E99.MirrorP", {"position": v(12.32, 38.1) * mm});
            skPoint(sketch, "E100.MirrorP", {"position": v(13.72, 38.1) * mm});
            skSolve(sketch);
        }
        {
            var Q0;
            Q0 = qSketchRegion(id + "F22", true);
            extrude(context, id + "F23", {"entities" : qUnion([Q0]), "operationType" : NewBodyOperationType.REMOVE, "oppositeDirection" : true, "depth" : 1.02 * mm, "offsetDistance" : 25.4 * mm});
        }
    });
